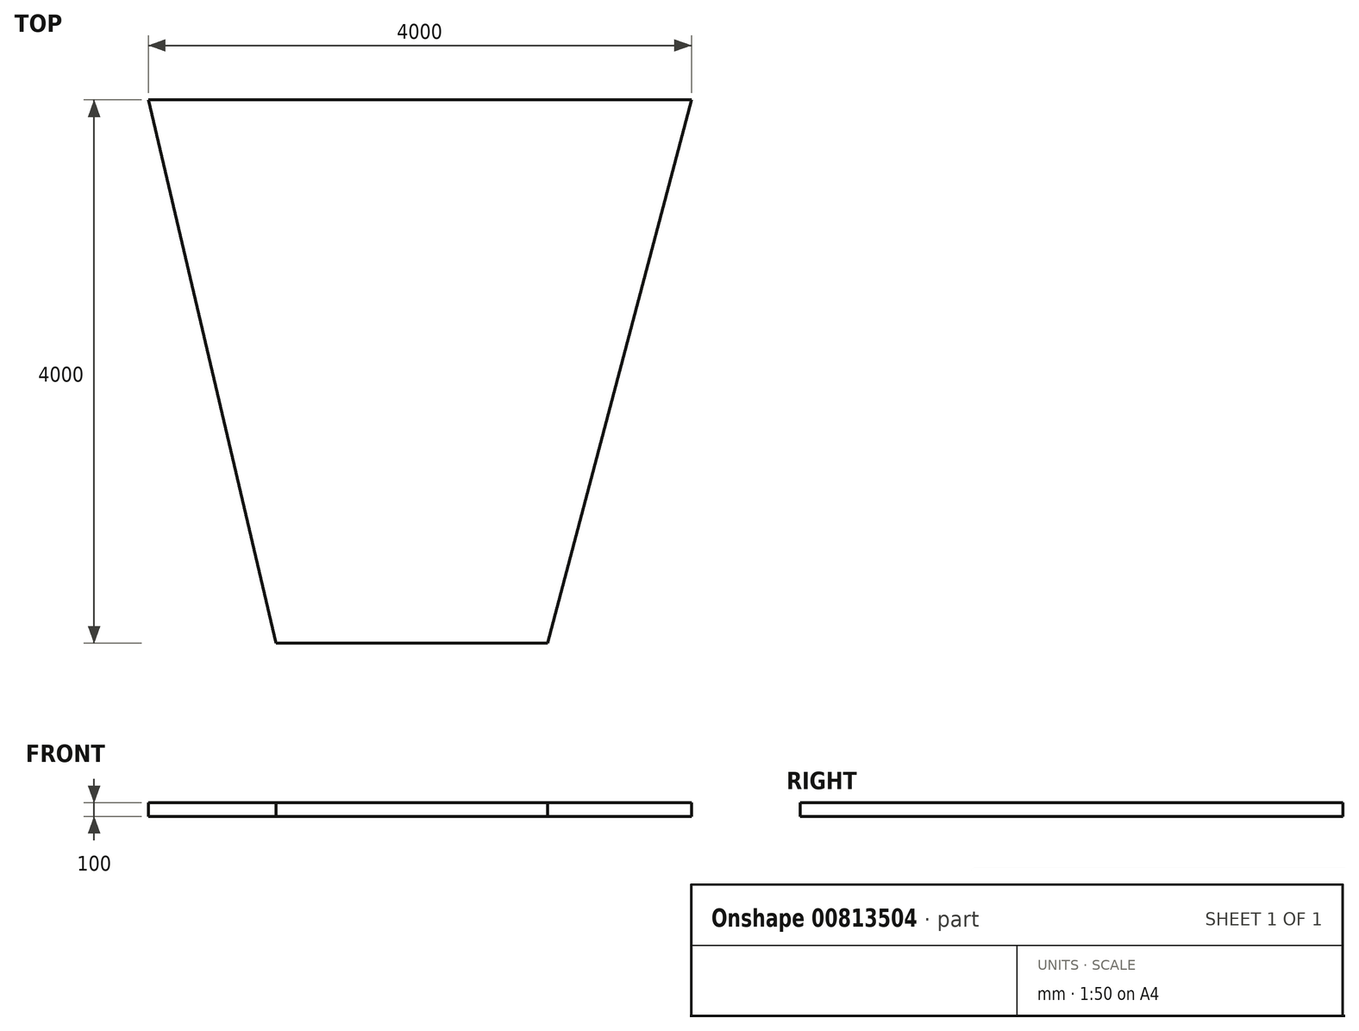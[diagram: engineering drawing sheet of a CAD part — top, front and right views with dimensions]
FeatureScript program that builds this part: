
annotation { "Feature Type Name" : "Feature", "Feature Type Description" : "" }
export const myFeature = defineFeature(function(context is Context, id is Id, definition is map)
    precondition{}
    {
        {
            var Q0;
            Q0=qCreatedBy(makeId("Top.planeOp"),FACE);
            var sketch = newSketch(context, id + "F0", { "sketchPlane" : qUnion([Q0])});
            skLineSegment(sketch, "E0", {"start": v(-1998.95, 1681.77) * mm, "end": v(2001.05, 1681.77) * mm});
            skLineSegment(sketch, "E1", {"start": v(2001.05, 1681.77) * mm, "end": v(940.56, -2318.23) * mm});
            skLineSegment(sketch, "E2", {"start": v(940.56, -2318.23) * mm, "end": v(-1059.44, -2318.23) * mm});
            skLineSegment(sketch, "E3", {"start": v(-1059.44, -2318.23) * mm, "end": v(-1998.95, 1681.77) * mm});
            skSolve(sketch);
        }
        {
            var Q0;
            Q0=makeQuery(id+"F0.imprint","IMPRINT",FACE,{"disambiguationData":[TD([[makeQuery(id+"F0.imprint","IMPRINT",EDGE,{"derivedFrom":sQuery(id+"F0.wireOp",EDGE,"E0")}),-1.0]])]});
            extrude(context, id + "F1", {"entities" : qUnion([Q0]), "depth" : 100 * mm, "offsetDistance" : 25 * mm});
        }
    });
